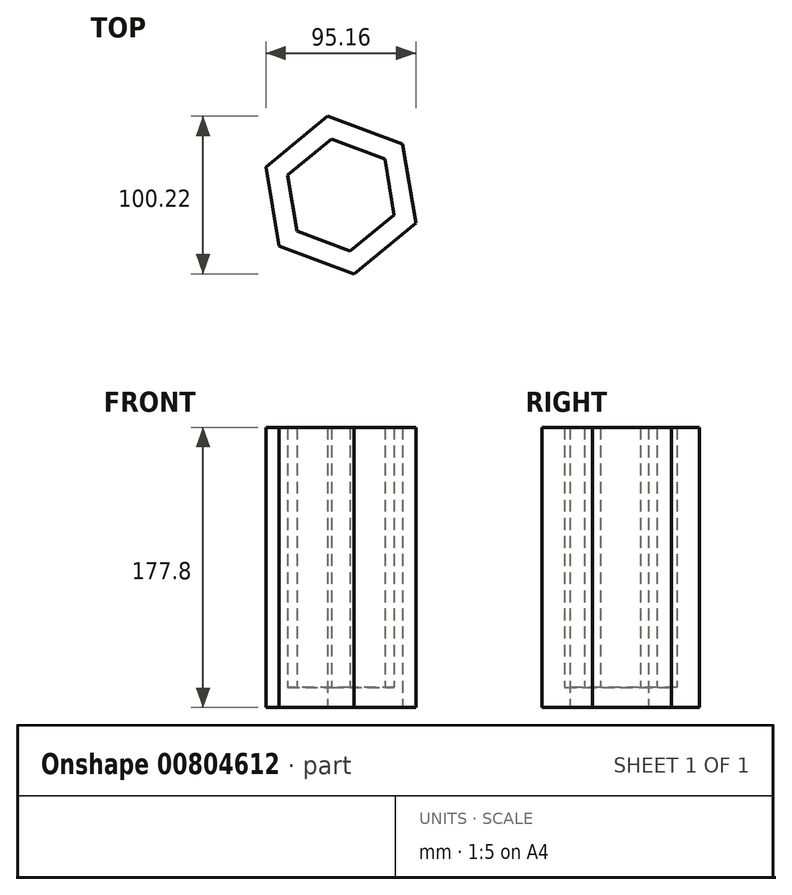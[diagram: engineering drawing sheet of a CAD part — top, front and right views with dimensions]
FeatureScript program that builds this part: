
annotation { "Feature Type Name" : "Feature", "Feature Type Description" : "" }
export const myFeature = defineFeature(function(context is Context, id is Id, definition is map)
    precondition{}
    {
        {
            var Q0;
            Q0=qCreatedBy(makeId("Top.planeOp"),FACE);
            var sketch = newSketch(context, id + "F0", { "sketchPlane" : qUnion([Q0])});
            skCircle(sketch, "E0.cCircle", {"center": v(0, 0) * mm, "radius": 44 * mm, "construction": true});
            skLineSegment(sketch, "E0.0", {"start": v(-8.37, 50.1) * mm, "end": v(39.21, 32.3) * mm});
            skLineSegment(sketch, "E0.1", {"start": v(39.21, 32.3) * mm, "end": v(47.58, -17.8) * mm});
            skLineSegment(sketch, "E0.2", {"start": v(47.58, -17.8) * mm, "end": v(8.37, -50.1) * mm});
            skLineSegment(sketch, "E0.3", {"start": v(8.37, -50.1) * mm, "end": v(-39.21, -32.3) * mm});
            skLineSegment(sketch, "E0.4", {"start": v(-39.21, -32.3) * mm, "end": v(-47.58, 17.8) * mm});
            skLineSegment(sketch, "E0.5", {"start": v(-47.58, 17.8) * mm, "end": v(-8.37, 50.1) * mm});
            skPoint(sketch, "E0.0.midPoint", {"position": v(15.42, 41.2) * mm});
            skSolve(sketch);
        }
        {
            var Q0;
            Q0=qSketchRegion(id+"F0",true);
            extrude(context, id + "F1", {"entities" : qUnion([Q0]), "depth" : 177.8 * mm, "offsetDistance" : 25.4 * mm});
        }
        {
            var Q0;
            Q0=makeQuery(id+"F1.opExtrude","CAP_FACE",FACE,{"disambiguationData":[OSD([sQuery(id+"F0.wireOp",EDGE,"E0.0"),sQuery(id+"F0.wireOp",EDGE,"E0.1"),sQuery(id+"F0.wireOp",EDGE,"E0.2"),sQuery(id+"F0.wireOp",EDGE,"E0.3"),sQuery(id+"F0.wireOp",EDGE,"E0.4"),sQuery(id+"F0.wireOp",EDGE,"E0.5")])],"isStart":false});
            shell(context, id + "F2", {"entities" : qUnion([Q0]), "thickness" : 12.7 * mm});
        }
    });
